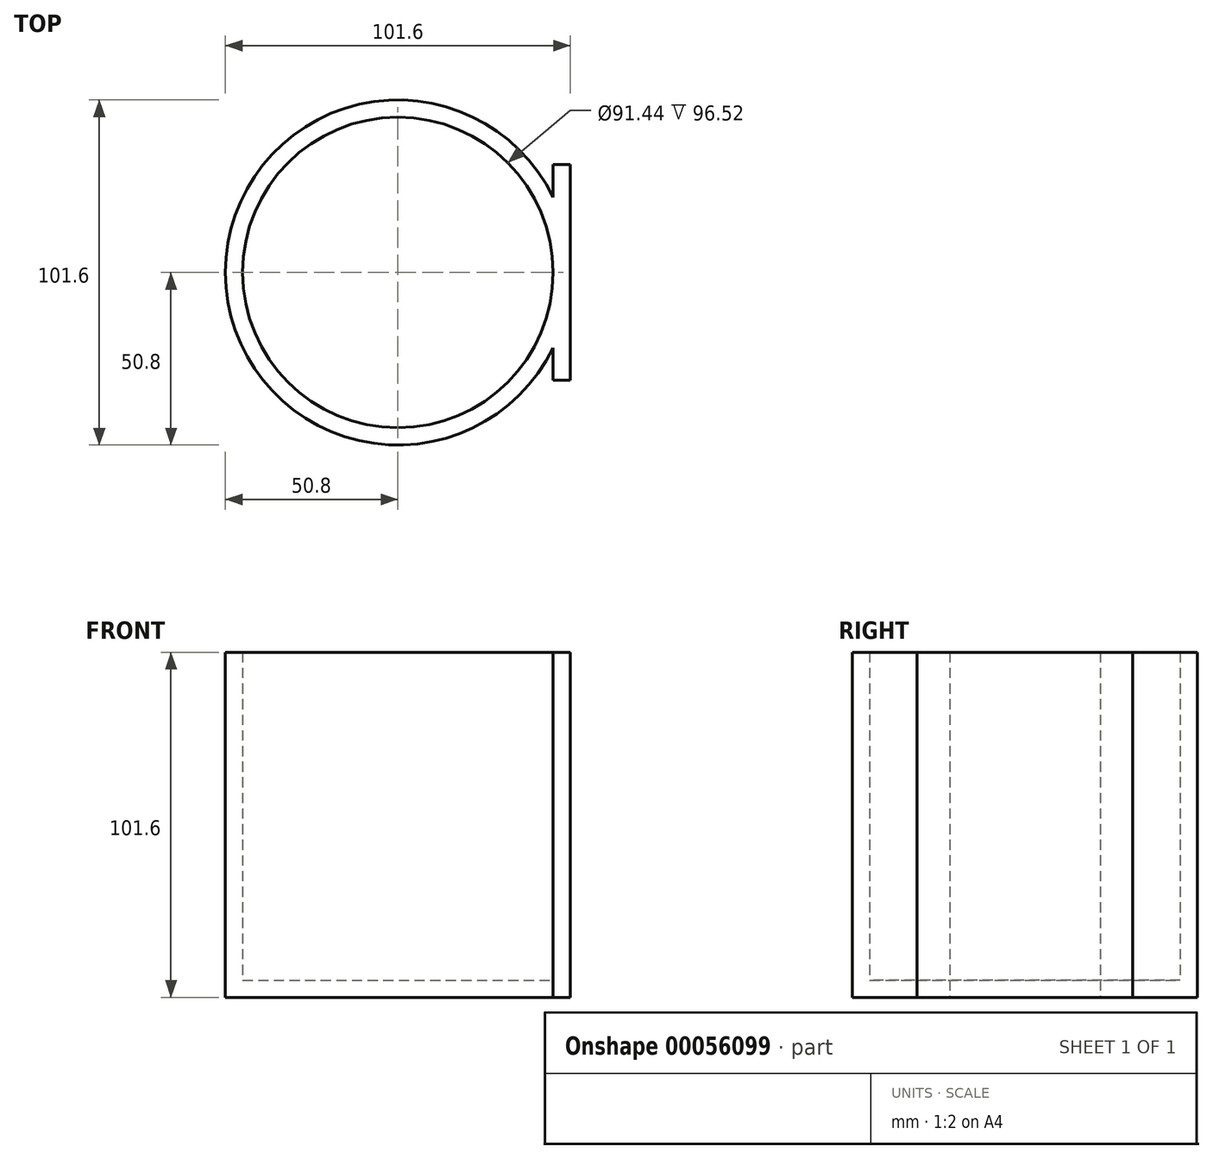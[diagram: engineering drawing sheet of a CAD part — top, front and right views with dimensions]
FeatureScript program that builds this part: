
annotation { "Feature Type Name" : "Feature", "Feature Type Description" : "" }
export const myFeature = defineFeature(function(context is Context, id is Id, definition is map)
    precondition{}
    {
        {
            var Q0;
            Q0=qCreatedBy(makeId("Front.planeOp"),FACE);
            var sketch = newSketch(context, id + "F0", { "sketchPlane" : qUnion([Q0])});
            skLineSegment(sketch, "E0.bottom", {"start": v(-50.8, 101.6) * mm, "end": v(-45.72, 101.6) * mm});
            skLineSegment(sketch, "E0.top", {"start": v(-50.8, 0) * mm, "end": v(-45.72, 0) * mm});
            skLineSegment(sketch, "E0.left", {"start": v(-50.8, 101.6) * mm, "end": v(-50.8, 0) * mm});
            skLineSegment(sketch, "E0.right", {"start": v(-45.72, 101.6) * mm, "end": v(-45.72, 5.08) * mm});
            skLineSegment(sketch, "E1.bottom", {"start": v(-45.72, 0) * mm, "end": v(0, 0) * mm});
            skLineSegment(sketch, "E1.top", {"start": v(-45.72, 5.08) * mm, "end": v(0, 5.08) * mm});
            skLineSegment(sketch, "E1.right", {"start": v(0, 0) * mm, "end": v(0, 5.08) * mm});
            skSolve(sketch);
        }
        {
            var Q0;
            Q0=qCreatedBy(makeId("Front.planeOp"),FACE);
            var sketch = newSketch(context, id + "F1", { "sketchPlane" : qUnion([Q0])});
            skLineSegment(sketch, "E2", {"start": v(0, 0) * mm, "end": v(0, 73.3) * mm});
            skSolve(sketch);
        }
        {
            var Q0;
            Q0 = qSketchRegion(id + "F0", true);
            var Q1;
            Q1=sQuery(id+"F1.wireOp",EDGE,"E2");
            revolve(context, id + "F2", {"entities" : qUnion([Q0]), "axis" : qUnion([Q1]), "revolveType" : RevolveType.FULL});
        }
        {
            var Q0;
            Q0=qCreatedBy(makeId("Right.planeOp"),FACE);
            cPlane(context, id + "F3", {"entities" : qUnion([Q0]), "cplaneType" : CPlaneType.OFFSET, "offset" : 50.8 * mm, "width" : 152.4 * mm, "height" : 152.4 * mm});
        }
        {
            var Q0;
            Q0=qCreatedBy(id+"F3.planeOp",FACE);
            var sketch = newSketch(context, id + "F4", { "sketchPlane" : qUnion([Q0])});
            skLineSegment(sketch, "E3.bottom", {"start": v(-31.75, 101.6) * mm, "end": v(31.75, 101.6) * mm});
            skLineSegment(sketch, "E3.top", {"start": v(-31.75, 0) * mm, "end": v(31.75, 0) * mm});
            skLineSegment(sketch, "E3.left", {"start": v(-31.75, 101.6) * mm, "end": v(-31.75, 0) * mm});
            skLineSegment(sketch, "E3.right", {"start": v(31.75, 101.6) * mm, "end": v(31.75, 0) * mm});
            skSolve(sketch);
        }
        {
            var Q0;
            Q0 = qSketchRegion(id + "F4", true);
            extrude(context, id + "F5", {"entities" : qUnion([Q0]), "operationType" : NewBodyOperationType.ADD, "oppositeDirection" : true, "depth" : 5.08 * mm});
        }
    });
